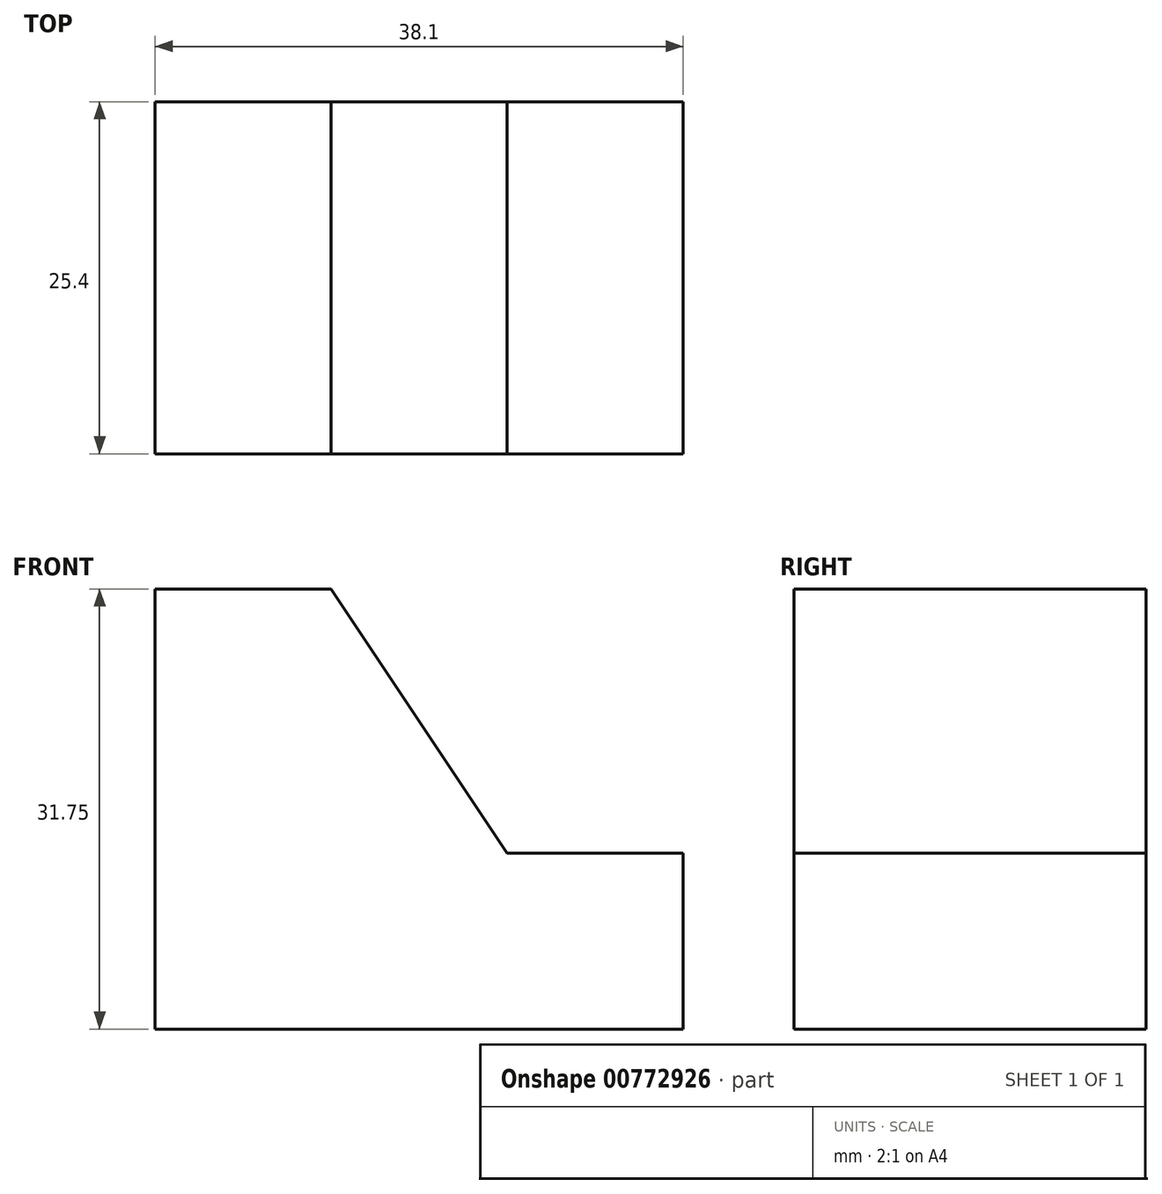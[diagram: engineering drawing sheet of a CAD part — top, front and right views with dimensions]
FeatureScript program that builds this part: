
annotation { "Feature Type Name" : "Feature", "Feature Type Description" : "" }
export const myFeature = defineFeature(function(context is Context, id is Id, definition is map)
    precondition{}
    {
        {
            var Q0;
            Q0=qCreatedBy(makeId("Front.planeOp"),FACE);
            var sketch = newSketch(context, id + "F0", { "sketchPlane" : qUnion([Q0])});
            skLineSegment(sketch, "E0", {"start": v(0, 0) * mm, "end": v(38.1, 0) * mm});
            skLineSegment(sketch, "E1", {"start": v(38.1, 0) * mm, "end": v(38.1, 31.75) * mm});
            skLineSegment(sketch, "E2", {"start": v(38.1, 31.75) * mm, "end": v(0, 31.75) * mm});
            skLineSegment(sketch, "E3", {"start": v(0, 31.75) * mm, "end": v(0, 0) * mm});
            skSolve(sketch);
        }
        {
            var Q0;
            Q0 = qSketchRegion(id + "F0", true);
            extrude(context, id + "F1", {"entities" : qUnion([Q0]), "depth" : 25.4 * mm, "offsetDistance" : 25.4 * mm});
        }
        {
            var Q0;
            Q0=makeQuery(id+"F1.opExtrude","CAP_FACE",FACE,{"disambiguationData":[OSD([sQuery(id+"F0.wireOp",EDGE,"E0"),sQuery(id+"F0.wireOp",EDGE,"E1"),sQuery(id+"F0.wireOp",EDGE,"E2"),sQuery(id+"F0.wireOp",EDGE,"E3")])],"isStart":false});
            var sketch = newSketch(context, id + "F2", { "sketchPlane" : qUnion([Q0])});
            skLineSegment(sketch, "E4", {"start": v(38.1, 0) * mm, "end": v(38.1, 12.7) * mm});
            skLineSegment(sketch, "E5", {"start": v(38.1, 12.7) * mm, "end": v(25.4, 12.7) * mm});
            skLineSegment(sketch, "E6", {"start": v(0, 31.75) * mm, "end": v(12.7, 31.75) * mm});
            skLineSegment(sketch, "E7", {"start": v(12.7, 31.75) * mm, "end": v(25.4, 12.7) * mm});
            skSolve(sketch);
        }
        {
            var Q0;
            {var subQ0=sQuery(id+"F2.wireOp",EDGE,"E5");Q0=makeQuery(id+"F2.imprint","IMPRINT",FACE,{"disambiguationData":[TD([[makeQuery(id+"F2.imprint","IMPRINT",EDGE,{"derivedFrom":subQ0}),-1.0]])]});}
            extrude(context, id + "F3", {"entities" : qUnion([Q0]), "operationType" : NewBodyOperationType.REMOVE, "oppositeDirection" : true, "depth" : 25.4 * mm, "offsetDistance" : 25.4 * mm});
        }
    });
